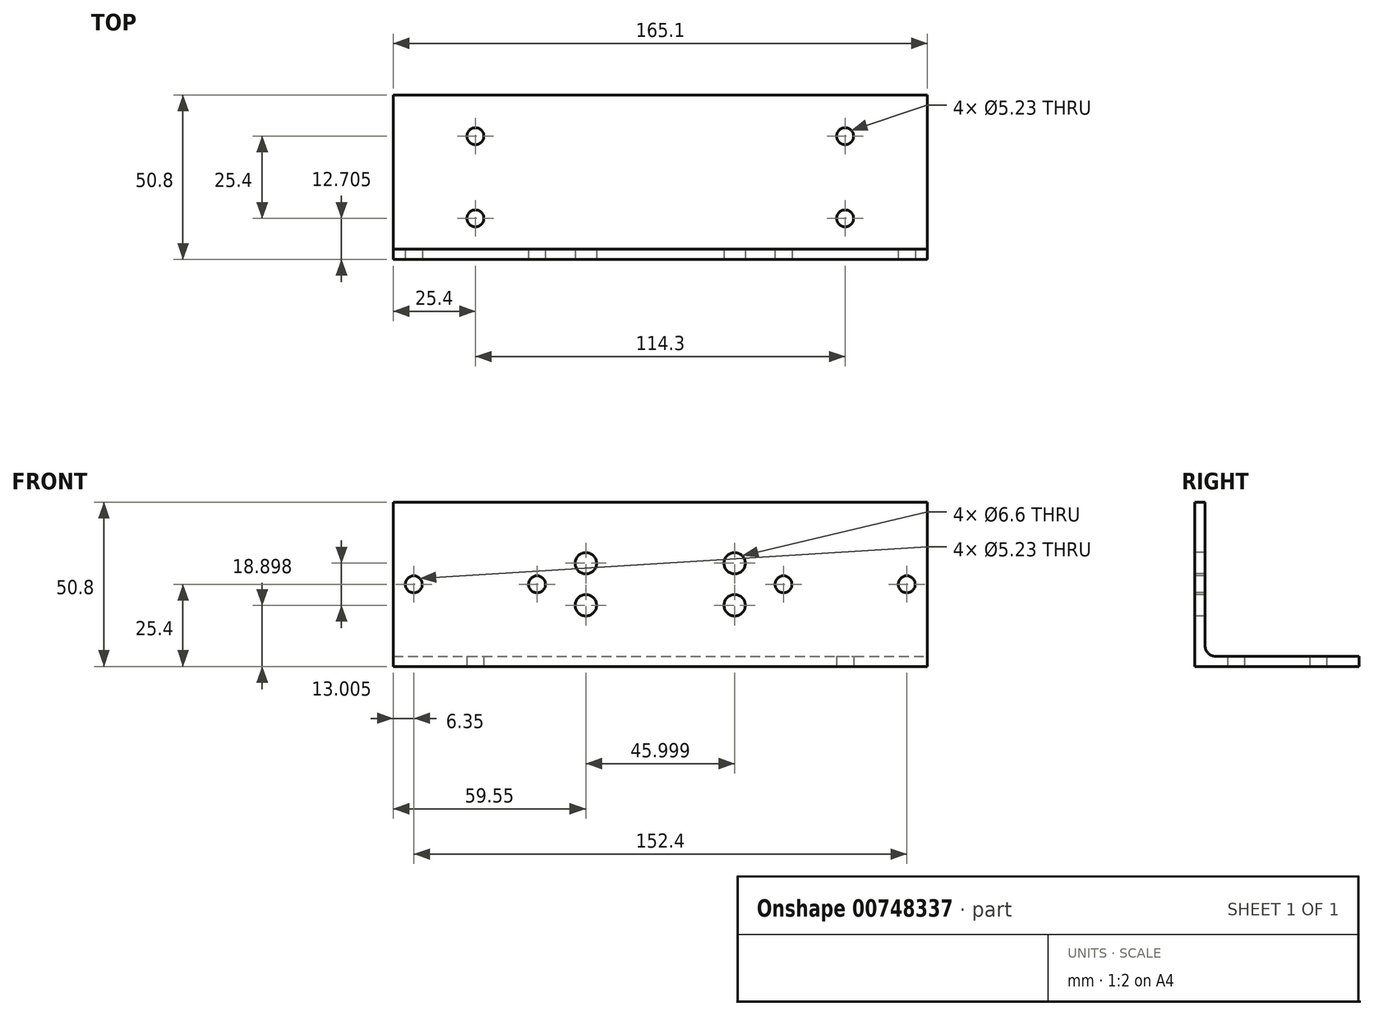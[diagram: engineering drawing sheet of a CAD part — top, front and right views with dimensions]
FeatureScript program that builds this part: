
annotation { "Feature Type Name" : "Feature", "Feature Type Description" : "" }
export const myFeature = defineFeature(function(context is Context, id is Id, definition is map)
    precondition{}
    {
        {
            var Q0;
            Q0=qCreatedBy(makeId("Right.planeOp"),FACE);
            var sketch = newSketch(context, id + "F0", { "sketchPlane" : qUnion([Q0])});
            skLineSegment(sketch, "E0", {"start": v(0, 0) * mm, "end": v(0, -44.45) * mm});
            skLineSegment(sketch, "E1", {"start": v(3.18, -47.63) * mm, "end": v(47.63, -47.62) * mm});
            skLineSegment(sketch, "E2.0", {"start": v(-3.17, -50.8) * mm, "end": v(47.63, -50.8) * mm});
            skLineSegment(sketch, "E2.1", {"start": v(-3.18, 0) * mm, "end": v(-3.17, -50.8) * mm});
            skLineSegment(sketch, "E3", {"start": v(-3.18, 0) * mm, "end": v(0, 0) * mm});
            skLineSegment(sketch, "E4", {"start": v(47.63, -47.62) * mm, "end": v(47.63, -50.8) * mm});
            skPoint(sketch, "E5.visualSharp", {"position": v(0, -47.63) * mm});
            skArc(sketch, "E5.filletArc", {"start": v(0, -44.45) * mm, "mid": v(0.93, -46.7) * mm, "end": v(3.18, -47.63) * mm});
            skSolve(sketch);
        }
        {
            var Q0;
            Q0=makeQuery(id+"F0.imprint","IMPRINT",FACE,{"disambiguationData":[TD([[makeQuery(id+"F0.imprint","IMPRINT",EDGE,{"derivedFrom":sQuery(id+"F0.wireOp",EDGE,"E0")}),-1.0]])]});
            extrude(context, id + "F1", {"entities" : qUnion([Q0]), "oppositeDirection" : true, "depth" : 165.1 * mm, "offsetDistance" : 25.4 * mm});
        }
        {
            var Q0;
            Q0=makeQuery(id+"F1.opExtrude","SWEPT_FACE",FACE,{"disambiguationData":[OSD([sQuery(id+"F0.wireOp",EDGE,"E2.1")])]});
            var sketch = newSketch(context, id + "F2", { "sketchPlane" : qUnion([Q0])});
            skLineSegment(sketch, "E6", {"start": v(-82.55, 0) * mm, "end": v(-82.55, -50.8) * mm, "construction": true});
            skLineSegment(sketch, "E7", {"start": v(0, -25.4) * mm, "end": v(-165.1, -25.4) * mm, "construction": true});
            skLineSegment(sketch, "E8", {"start": v(-25.4, 0) * mm, "end": v(-25.4, -50.8) * mm, "construction": true});
            skLineSegment(sketch, "E9", {"start": v(-139.7, 0) * mm, "end": v(-139.7, -50.8) * mm, "construction": true});
            skLineSegment(sketch, "E10.0", {"start": v(-158.75, 0) * mm, "end": v(-158.75, -50.8) * mm, "construction": true});
            skLineSegment(sketch, "E11.0", {"start": v(-120.65, 0) * mm, "end": v(-120.65, -50.8) * mm, "construction": true});
            skLineSegment(sketch, "E12.0", {"start": v(-44.45, 0) * mm, "end": v(-44.45, -50.8) * mm, "construction": true});
            skLineSegment(sketch, "E13.0", {"start": v(-6.35, 0) * mm, "end": v(-6.35, -50.8) * mm, "construction": true});
            skCircle(sketch, "E14", {"center": v(-158.75, -25.4) * mm, "radius": 2.62 * mm});
            skCircle(sketch, "E15", {"center": v(-120.65, -25.4) * mm, "radius": 2.62 * mm});
            skCircle(sketch, "E16", {"center": v(-44.45, -25.4) * mm, "radius": 2.62 * mm});
            skCircle(sketch, "E17", {"center": v(-6.35, -25.4) * mm, "radius": 2.62 * mm});
            skLineSegment(sketch, "E18.0", {"start": v(-105.55, 0) * mm, "end": v(-105.55, -50.8) * mm, "construction": true});
            skLineSegment(sketch, "E19.0", {"start": v(-59.55, 0) * mm, "end": v(-59.55, -50.8) * mm, "construction": true});
            skLineSegment(sketch, "E20.0", {"start": v(0, -18.9) * mm, "end": v(-152.4, -18.9) * mm, "construction": true});
            skLineSegment(sketch, "E21.0", {"start": v(0, -31.9) * mm, "end": v(-152.4, -31.9) * mm, "construction": true});
            skCircle(sketch, "E22", {"center": v(-59.55, -31.9) * mm, "radius": 3.3 * mm});
            skCircle(sketch, "E23", {"center": v(-105.55, -31.9) * mm, "radius": 3.3 * mm});
            skCircle(sketch, "E24", {"center": v(-59.55, -18.9) * mm, "radius": 3.3 * mm});
            skCircle(sketch, "E25", {"center": v(-105.55, -18.9) * mm, "radius": 3.3 * mm});
            skSolve(sketch);
        }
        {
            var Q0;
            Q0 = qSketchRegion(id + "F2", true);
            extrude(context, id + "F3", {"entities" : qUnion([Q0]), "operationType" : NewBodyOperationType.REMOVE, "endBound" : BoundingType.THROUGH_ALL, "oppositeDirection" : true, "depth" : 25.4 * mm, "offsetDistance" : 25.4 * mm});
        }
        {
            var Q0;
            Q0=makeQuery(id+"F1.opExtrude","SWEPT_FACE",FACE,{"disambiguationData":[OSD([sQuery(id+"F0.wireOp",EDGE,"E2.0")])]});
            var sketch = newSketch(context, id + "F4", { "sketchPlane" : qUnion([Q0])});
            skLineSegment(sketch, "E26", {"start": v(0, -22.23) * mm, "end": v(-165.1, -22.23) * mm, "construction": true});
            skLineSegment(sketch, "E27", {"start": v(-82.55, -47.63) * mm, "end": v(-82.55, 3.18) * mm, "construction": true});
            skLineSegment(sketch, "E28", {"start": v(-82.55, 3.18) * mm, "end": v(-83.2, 2.14) * mm, "construction": true});
            skLineSegment(sketch, "E29", {"start": v(-120.65, -47.63) * mm, "end": v(-119.8, -49.25) * mm, "construction": true});
            skLineSegment(sketch, "E30", {"start": v(-139.7, -47.63) * mm, "end": v(-139.7, 3.18) * mm, "construction": true});
            skLineSegment(sketch, "E31", {"start": v(-25.4, -47.63) * mm, "end": v(-25.4, 3.18) * mm, "construction": true});
            skLineSegment(sketch, "E32", {"start": v(0, -34.92) * mm, "end": v(-165.1, -34.92) * mm, "construction": true});
            skLineSegment(sketch, "E33", {"start": v(0, -9.53) * mm, "end": v(-165.1, -9.53) * mm, "construction": true});
            skCircle(sketch, "E34", {"center": v(-25.4, -34.92) * mm, "radius": 2.62 * mm});
            skCircle(sketch, "E35", {"center": v(-25.4, -9.53) * mm, "radius": 2.62 * mm});
            skCircle(sketch, "E36", {"center": v(-139.7, -34.92) * mm, "radius": 2.62 * mm});
            skCircle(sketch, "E37", {"center": v(-139.7, -9.53) * mm, "radius": 2.62 * mm});
            skSolve(sketch);
        }
        {
            var Q0;
            Q0 = qSketchRegion(id + "F4", true);
            extrude(context, id + "F5", {"entities" : qUnion([Q0]), "operationType" : NewBodyOperationType.REMOVE, "oppositeDirection" : true, "depth" : 25.4 * mm, "offsetDistance" : 25.4 * mm});
        }
    });
